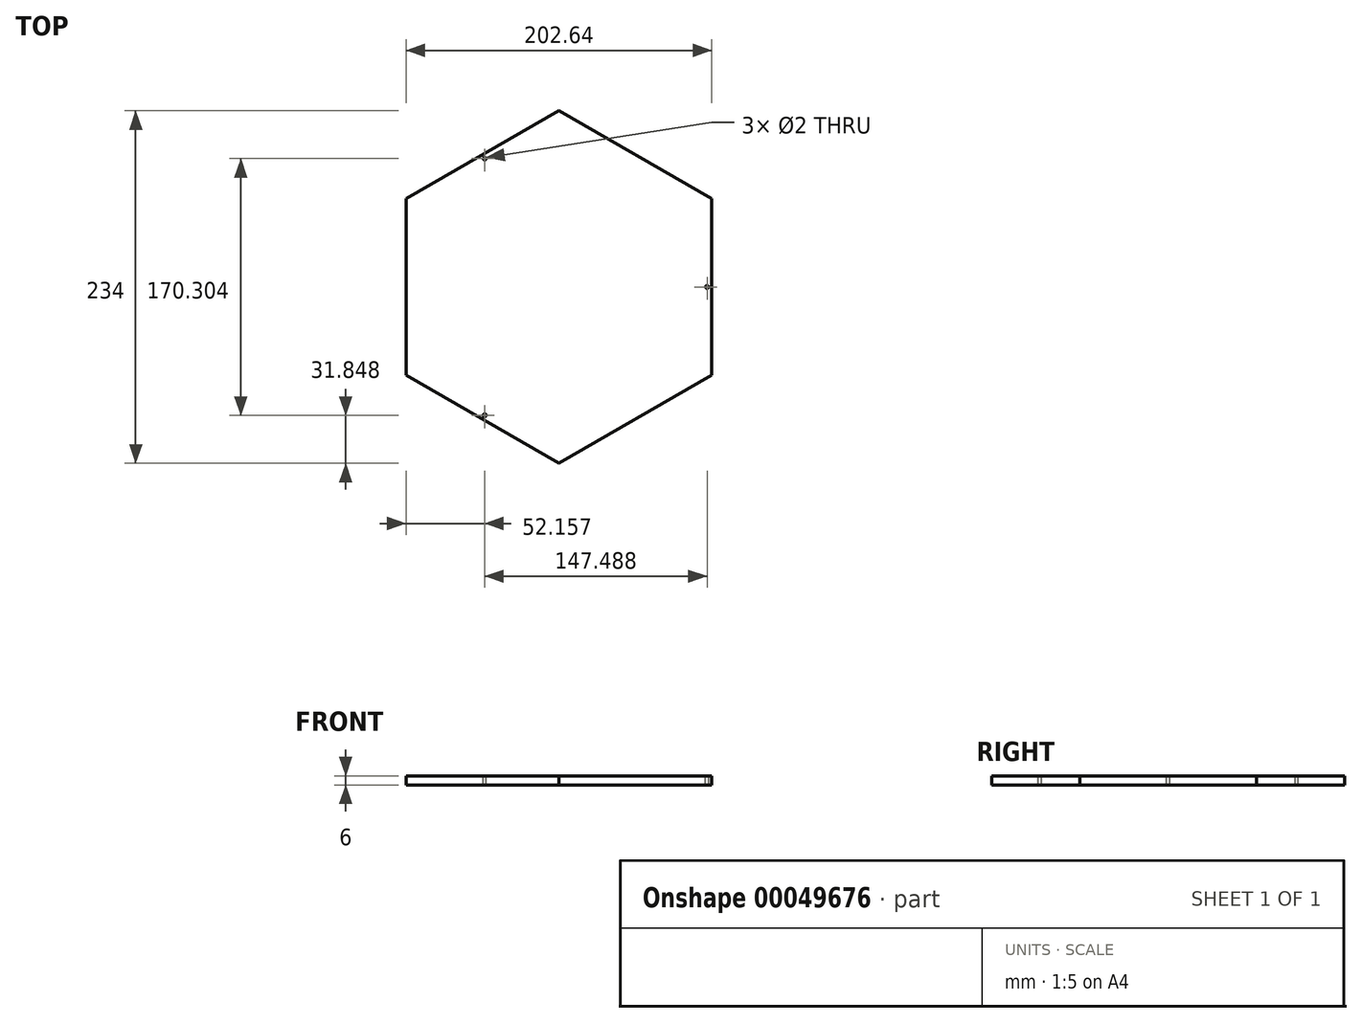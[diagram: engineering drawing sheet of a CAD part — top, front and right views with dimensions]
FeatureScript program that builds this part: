
annotation { "Feature Type Name" : "Feature", "Feature Type Description" : "" }
export const myFeature = defineFeature(function(context is Context, id is Id, definition is map)
    precondition{}
    {
        {
            var Q0;
            Q0=qCreatedBy(makeId("Top.planeOp"),FACE);
            var sketch = newSketch(context, id + "F0", { "sketchPlane" : qUnion([Q0])});
            skCircle(sketch, "E0.cCircle", {"center": v(0, 0) * mm, "radius": 101.32 * mm, "construction": true});
            skLineSegment(sketch, "E0.0", {"start": v(101.32, -58.5) * mm, "end": v(0, -117) * mm});
            skLineSegment(sketch, "E0.1", {"start": v(0, -117) * mm, "end": v(-101.32, -58.5) * mm});
            skLineSegment(sketch, "E0.2", {"start": v(-101.32, -58.5) * mm, "end": v(-101.32, 58.5) * mm});
            skLineSegment(sketch, "E0.3", {"start": v(-101.32, 58.5) * mm, "end": v(0, 117) * mm});
            skLineSegment(sketch, "E0.4", {"start": v(0, 117) * mm, "end": v(101.32, 58.5) * mm});
            skLineSegment(sketch, "E0.5", {"start": v(101.32, 58.5) * mm, "end": v(101.32, -58.5) * mm});
            skPoint(sketch, "E0.0.midPoint", {"position": v(50.66, -87.75) * mm});
            skLineSegment(sketch, "E1", {"start": v(0, 117) * mm, "end": v(0, -117) * mm, "construction": true});
            skSolve(sketch);
        }
        {
            var Q0;
            Q0 = qSketchRegion(id + "F0", true);
            extrude(context, id + "F1", {"entities" : qUnion([Q0]), "depth" : 6 * mm});
        }
        {
            var Q0;
            Q0=makeQuery(id+"F1.opExtrude","CAP_FACE",FACE,{"disambiguationData":[OSD([sQuery(id+"F0.wireOp",EDGE,"E0.0"),sQuery(id+"F0.wireOp",EDGE,"E0.1"),sQuery(id+"F0.wireOp",EDGE,"E0.2"),sQuery(id+"F0.wireOp",EDGE,"E0.3"),sQuery(id+"F0.wireOp",EDGE,"E0.4"),sQuery(id+"F0.wireOp",EDGE,"E0.5")])],"isStart":false});
            var sketch = newSketch(context, id + "F2", { "sketchPlane" : qUnion([Q0])});
            skLineSegment(sketch, "E2", {"start": v(101.32, 0) * mm, "end": v(98.32, 0) * mm, "construction": true});
            skLineSegment(sketch, "E3", {"start": v(-50.66, 87.75) * mm, "end": v(-49.16, 85.15) * mm, "construction": true});
            skLineSegment(sketch, "E4", {"start": v(-50.66, -87.75) * mm, "end": v(-49.16, -85.15) * mm, "construction": true});
            skCircle(sketch, "E5", {"center": v(-49.16, -85.15) * mm, "radius": 1 * mm});
            skCircle(sketch, "E6", {"center": v(-49.16, 85.15) * mm, "radius": 1 * mm});
            skCircle(sketch, "E7", {"center": v(98.32, 0) * mm, "radius": 1 * mm});
            skSolve(sketch);
        }
        {
            var Q0;
            Q0 = qSketchRegion(id + "F2", true);
            extrude(context, id + "F3", {"entities" : qUnion([Q0]), "operationType" : NewBodyOperationType.REMOVE, "oppositeDirection" : true, "depth" : 25 * mm});
        }
    });
